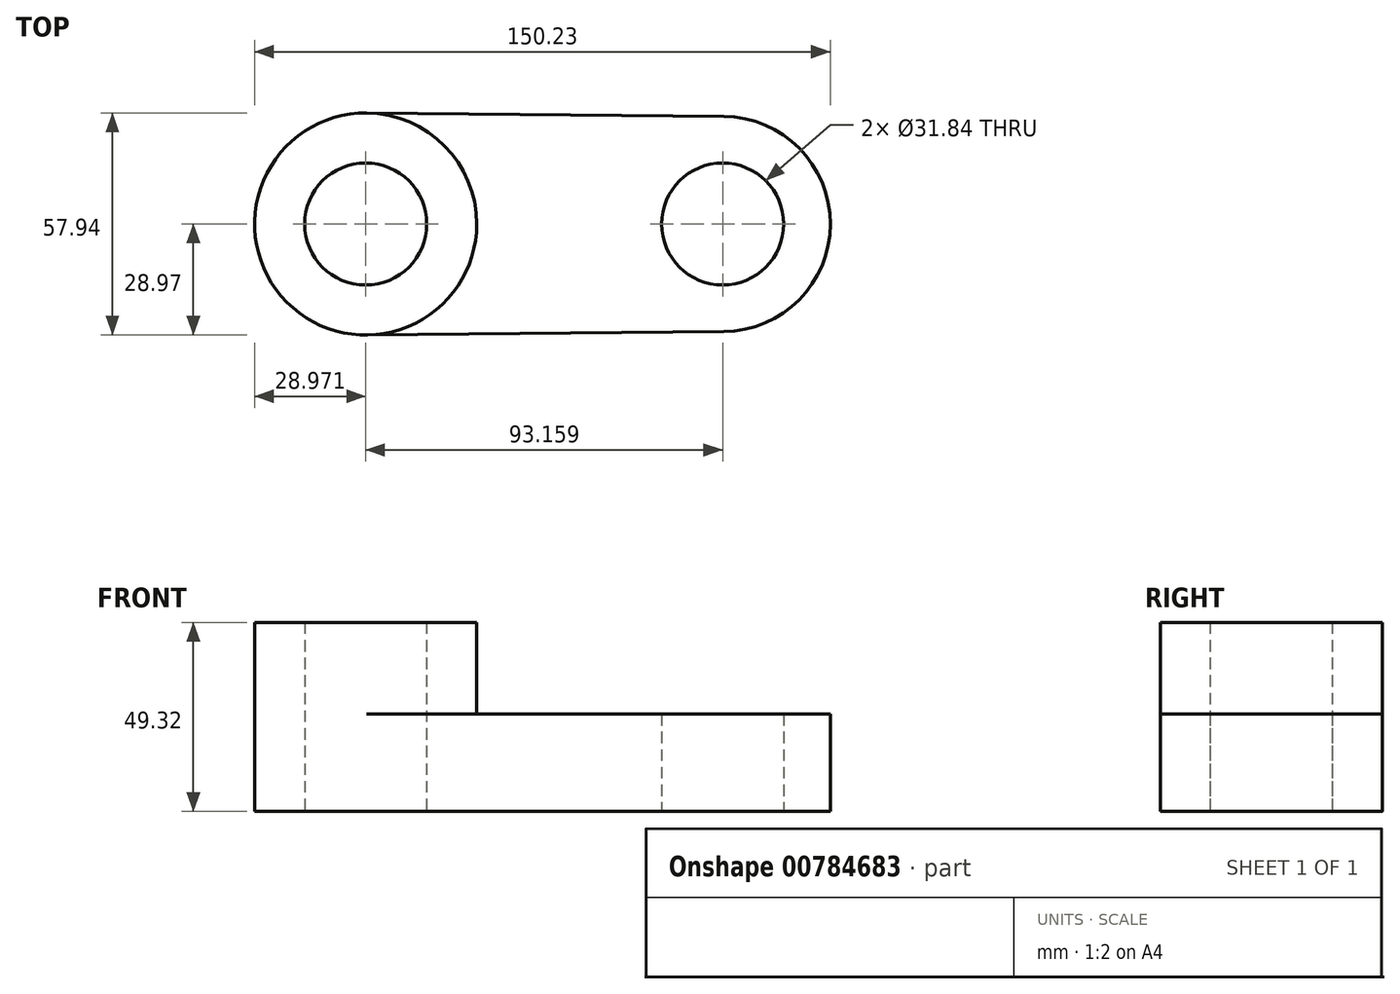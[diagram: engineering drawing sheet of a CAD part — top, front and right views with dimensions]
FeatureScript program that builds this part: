
annotation { "Feature Type Name" : "Feature", "Feature Type Description" : "" }
export const myFeature = defineFeature(function(context is Context, id is Id, definition is map)
    precondition{}
    {
        {
            var Q0;
            Q0=qCreatedBy(makeId("Top.planeOp"),FACE);
            var sketch = newSketch(context, id + "F0", { "sketchPlane" : qUnion([Q0])});
            skCircle(sketch, "E0", {"center": v(-46.58, 0) * mm, "radius": 15.92 * mm});
            skCircle(sketch, "E1", {"center": v(46.58, 0) * mm, "radius": 15.92 * mm});
            skArc(sketch, "E2", {"start": v(-46.3, 28.97) * mm, "mid": v(-75.55, 0) * mm, "end": v(-46.3, -28.97) * mm});
            skArc(sketch, "E3", {"start": v(46.84, -28.1) * mm, "mid": v(74.68, 0) * mm, "end": v(46.84, 28.1) * mm});
            skLineSegment(sketch, "E4", {"start": v(-46.3, 28.97) * mm, "end": v(46.84, 28.1) * mm});
            skLineSegment(sketch, "E5", {"start": v(46.84, -28.1) * mm, "end": v(-46.3, -28.97) * mm});
            skArc(sketch, "E6", {"start": v(-46.3, -28.97) * mm, "mid": v(-17.6, 0) * mm, "end": v(-46.3, 28.97) * mm});
            skSolve(sketch);
        }
        {
            var Q0;
            Q0=makeQuery(id+"F0.imprint","IMPRINT",FACE,{"disambiguationData":[TD([[makeQuery(id+"F0.imprint","IMPRINT",EDGE,{"derivedFrom":sQuery(id+"F0.wireOp",EDGE,"E0")}),-1.0]])]});
            var Q1;
            Q1=makeQuery(id+"F0.imprint","IMPRINT",FACE,{"disambiguationData":[TD([[makeQuery(id+"F0.imprint","IMPRINT",EDGE,{"derivedFrom":sQuery(id+"F0.wireOp",EDGE,"E1")}),-1.0]])]});
            extrude(context, id + "F1", {"entities" : qUnion([Q0, Q1]), "depth" : 25.4 * mm});
        }
        {
            var Q0;
            Q0=makeQuery(id+"F0.imprint","IMPRINT",FACE,{"disambiguationData":[TD([[makeQuery(id+"F0.imprint","IMPRINT",EDGE,{"derivedFrom":sQuery(id+"F0.wireOp",EDGE,"E0")}),-1.0]])]});
            extrude(context, id + "F2", {"entities" : qUnion([Q0]), "operationType" : NewBodyOperationType.ADD, "depth" : 49.32 * mm, "offsetDistance" : 25.4 * mm});
        }
    });
